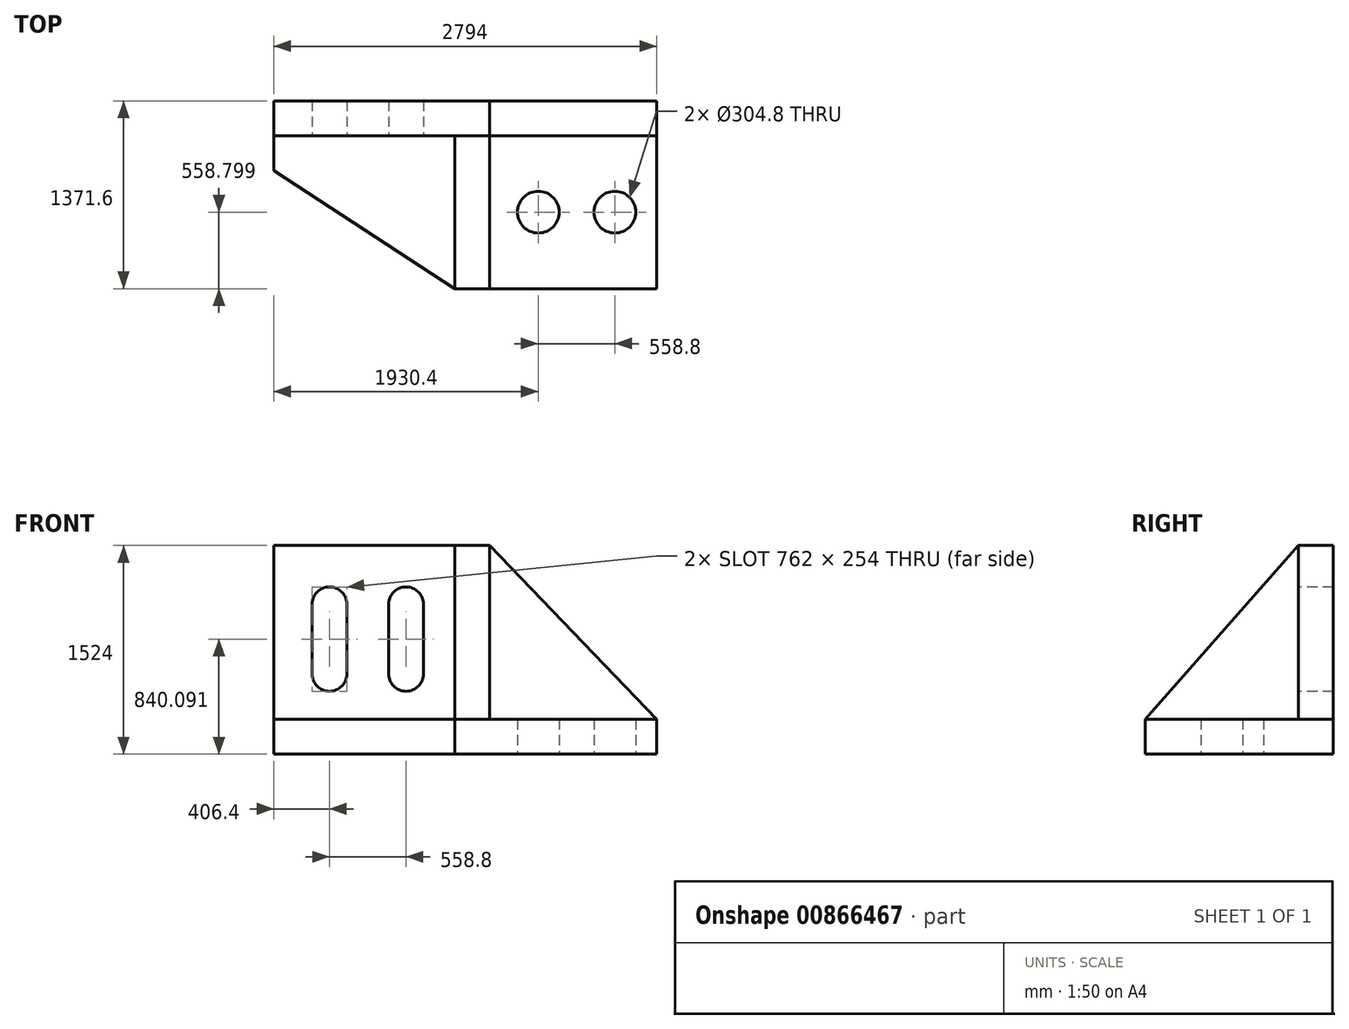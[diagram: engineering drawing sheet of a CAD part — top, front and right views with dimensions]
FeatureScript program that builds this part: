
annotation { "Feature Type Name" : "Feature", "Feature Type Description" : "" }
export const myFeature = defineFeature(function(context is Context, id is Id, definition is map)
    precondition{}
    {
        {
            var Q0;
            Q0=qCreatedBy(makeId("Top.planeOp"),FACE);
            var sketch = newSketch(context, id + "F0", { "sketchPlane" : qUnion([Q0])});
            skLineSegment(sketch, "E0", {"start": v(-1397, 579.58) * mm, "end": v(1397, 579.58) * mm});
            skLineSegment(sketch, "E1", {"start": v(1397, 579.58) * mm, "end": v(1397, -792.02) * mm});
            skLineSegment(sketch, "E2", {"start": v(1397, -792.02) * mm, "end": v(-76.2, -792.02) * mm});
            skLineSegment(sketch, "E3", {"start": v(-76.2, -792.02) * mm, "end": v(-1397, 71.58) * mm});
            skLineSegment(sketch, "E4", {"start": v(-1397, 71.58) * mm, "end": v(-1397, 579.58) * mm});
            skLineSegment(sketch, "E5", {"start": v(-76.2, -792.02) * mm, "end": v(-76.2, 579.58) * mm});
            skLineSegment(sketch, "E6", {"start": v(-76.2, 579.58) * mm, "end": v(177.8, 579.58) * mm});
            skLineSegment(sketch, "E7", {"start": v(177.8, 579.58) * mm, "end": v(177.8, -792.02) * mm});
            skLineSegment(sketch, "E8", {"start": v(-1397, 325.58) * mm, "end": v(1397, 325.58) * mm});
            skCircle(sketch, "E9", {"center": v(533.4, -233.22) * mm, "radius": 152.4 * mm});
            skCircle(sketch, "E10", {"center": v(1092.2, -233.22) * mm, "radius": 152.4 * mm});
            skSolve(sketch);
        }
        {
            var Q0;
            {var subQ0=sQuery(id+"F0.wireOp",EDGE,"E7");var subQ1=sQuery(id+"F0.wireOp",EDGE,"E0");var subQ2=makeQuery(id+"F0.imprint","INTERSECT",VERTEX,{"derivedFrom":[subQ1,subQ0]});Q0=makeQuery(id+"F0.imprint","IMPRINT",FACE,{"disambiguationData":[TD([[makeQuery(id+"F0.imprint","IMPRINT",EDGE,{"disambiguationData":[TD([[subQ2,-1.0]])],"derivedFrom":subQ1}),-1.0]])]});}
            var Q1;
            {var subQ3=sQuery(id+"F0.wireOp",EDGE,"E7");var subQ5=sQuery(id+"F0.wireOp",EDGE,"E8");var subQ6=makeQuery(id+"F0.imprint","INTERSECT",VERTEX,{"derivedFrom":[subQ3,subQ5]});Q1=makeQuery(id+"F0.imprint","IMPRINT",FACE,{"disambiguationData":[TD([[makeQuery(id+"F0.imprint","IMPRINT",EDGE,{"disambiguationData":[TD([[subQ6,-1.0]])],"derivedFrom":subQ3}),-1.0]])]});}
            var Q2;
            {var subQ0=sQuery(id+"F0.wireOp",EDGE,"E7");var subQ1=sQuery(id+"F0.wireOp",EDGE,"E0");var subQ2=makeQuery(id+"F0.imprint","INTERSECT",VERTEX,{"derivedFrom":[subQ1,subQ0]});Q2=makeQuery(id+"F0.imprint","IMPRINT",FACE,{"disambiguationData":[TD([[makeQuery(id+"F0.imprint","IMPRINT",EDGE,{"disambiguationData":[TD([[subQ2,1.0]])],"derivedFrom":subQ1}),-1.0]])]});}
            var Q3;
            {var subQ0=sQuery(id+"F0.wireOp",EDGE,"E4");var subQ1=sQuery(id+"F0.wireOp",EDGE,"E0");var subQ2=makeQuery(id+"F0.imprint","INTERSECT",VERTEX,{"derivedFrom":[subQ1,subQ0]});Q3=makeQuery(id+"F0.imprint","IMPRINT",FACE,{"disambiguationData":[TD([[makeQuery(id+"F0.imprint","IMPRINT",EDGE,{"disambiguationData":[TD([[subQ2,-1.0]])],"derivedFrom":subQ1}),-1.0]])]});}
            extrude(context, id + "F1", {"entities" : qUnion([Q0, Q1, Q2, Q3]), "depth" : 1524 * mm, "offsetDistance" : 25.4 * mm});
        }
        {
            var Q0;
            {var subQ0=sQuery(id+"F0.wireOp",EDGE,"E3");Q0=makeQuery(id+"F0.imprint","IMPRINT",FACE,{"disambiguationData":[TD([[makeQuery(id+"F0.imprint","IMPRINT",EDGE,{"derivedFrom":subQ0}),-1.0]])]});}
            var Q1;
            Q1=makeQuery(id+"F0.imprint","IMPRINT",FACE,{"disambiguationData":[TD([[makeQuery(id+"F0.imprint","IMPRINT",EDGE,{"derivedFrom":sQuery(id+"F0.wireOp",EDGE,"E9")}),-1.0]])]});
            extrude(context, id + "F2", {"entities" : qUnion([Q0, Q1]), "operationType" : NewBodyOperationType.ADD, "depth" : 254 * mm, "offsetDistance" : 25.4 * mm});
        }
        {
            var Q0;
            {var subQ0=sQuery(id+"F0.wireOp",EDGE,"E8");Q0=makeQuery(id+"F1.opExtrude","SWEPT_FACE",FACE,{"disambiguationData":[OSD([subQ0]),TDD([makeQuery(id+"F0.imprint","IMPRINT",EDGE,{"disambiguationData":[TD([[makeQuery(id+"F0.imprint","INTERSECT",VERTEX,{"derivedFrom":[sQuery(id+"F0.wireOp",EDGE,"E1"),subQ0]}),1.0]])],"derivedFrom":subQ0})])]});}
            var sketch = newSketch(context, id + "F3", { "sketchPlane" : qUnion([Q0])});
            skLineSegment(sketch, "E11", {"start": v(177.8, 1524) * mm, "end": v(1397, 254) * mm});
            skSolve(sketch);
        }
        {
            var Q0;
            Q0 = qSketchRegion(id + "F3", true);
            var Q1;
            Q1=makeQuery(id+"F3.imprint","IMPRINT",FACE,{"disambiguationData":[TD([[makeQuery(id+"F3.imprint","IMPRINT",EDGE,{"derivedFrom":sQuery(id+"F3.wireOp",EDGE,"E11")}),1.0]])]});
            extrude(context, id + "F4", {"entities" : qUnion([Q0, Q1]), "operationType" : NewBodyOperationType.REMOVE, "oppositeDirection" : true, "depth" : 891.54 * mm, "offsetDistance" : 25.4 * mm});
        }
        {
            var Q0;
            Q0=makeQuery(id+"F1.opExtrude","SWEPT_FACE",FACE,{"disambiguationData":[OSD([sQuery(id+"F0.wireOp",EDGE,"E7")])]});
            var sketch = newSketch(context, id + "F5", { "sketchPlane" : qUnion([Q0])});
            skLineSegment(sketch, "E12", {"start": v(325.58, 1524) * mm, "end": v(-792.02, 254) * mm});
            skSolve(sketch);
        }
        {
            var Q0;
            Q0 = qSketchRegion(id + "F5", true);
            var Q1;
            Q1=makeQuery(id+"F5.imprint","IMPRINT",FACE,{"disambiguationData":[TD([[makeQuery(id+"F5.imprint","IMPRINT",EDGE,{"derivedFrom":sQuery(id+"F5.wireOp",EDGE,"E12")}),-1.0]])]});
            extrude(context, id + "F6", {"entities" : qUnion([Q0, Q1]), "operationType" : NewBodyOperationType.REMOVE, "oppositeDirection" : true, "depth" : 1061.72 * mm, "offsetDistance" : 25.4 * mm});
        }
        {
            var Q0;
            {var subQ0=sQuery(id+"F0.wireOp",EDGE,"E8");Q0=makeQuery(id+"F1.opExtrude","SWEPT_FACE",FACE,{"disambiguationData":[OSD([subQ0]),TDD([makeQuery(id+"F0.imprint","IMPRINT",EDGE,{"disambiguationData":[TD([[makeQuery(id+"F0.imprint","INTERSECT",VERTEX,{"derivedFrom":[sQuery(id+"F0.wireOp",EDGE,"E4"),subQ0]}),-1.0]])],"derivedFrom":subQ0})])]});}
            var sketch = newSketch(context, id + "F7", { "sketchPlane" : qUnion([Q0])});
            skArc(sketch, "E13", {"start": v(-863.6, 1094.1) * mm, "mid": v(-990.6, 1221.1) * mm, "end": v(-1117.6, 1094.1) * mm});
            skArc(sketch, "E14", {"start": v(-304.8, 1094.1) * mm, "mid": v(-431.8, 1221.1) * mm, "end": v(-558.8, 1094.1) * mm});
            skArc(sketch, "E15", {"start": v(-1117.6, 586.1) * mm, "mid": v(-990.6, 459.1) * mm, "end": v(-863.6, 586.1) * mm});
            skArc(sketch, "E16", {"start": v(-558.8, 586.1) * mm, "mid": v(-431.8, 459.1) * mm, "end": v(-304.8, 586.1) * mm});
            skLineSegment(sketch, "E17", {"start": v(-1117.6, 1094.1) * mm, "end": v(-1117.6, 586.1) * mm});
            skLineSegment(sketch, "E18", {"start": v(-863.6, 1094.1) * mm, "end": v(-863.6, 586.1) * mm});
            skLineSegment(sketch, "E19", {"start": v(-558.8, 1094.1) * mm, "end": v(-558.8, 586.1) * mm});
            skLineSegment(sketch, "E20", {"start": v(-304.8, 1094.1) * mm, "end": v(-304.8, 586.1) * mm});
            skSolve(sketch);
        }
        {
            var Q0;
            Q0=makeQuery(id+"F7.imprint","IMPRINT",FACE,{"disambiguationData":[TD([[makeQuery(id+"F7.imprint","IMPRINT",EDGE,{"derivedFrom":sQuery(id+"F7.wireOp",EDGE,"E14")}),1.0]])]});
            var Q1;
            Q1=makeQuery(id+"F7.imprint","IMPRINT",FACE,{"disambiguationData":[TD([[makeQuery(id+"F7.imprint","IMPRINT",EDGE,{"derivedFrom":sQuery(id+"F7.wireOp",EDGE,"E13")}),1.0]])]});
            extrude(context, id + "F8", {"entities" : qUnion([Q0, Q1]), "operationType" : NewBodyOperationType.REMOVE, "oppositeDirection" : true, "depth" : 688.34 * mm, "offsetDistance" : 25.4 * mm});
        }
    });
